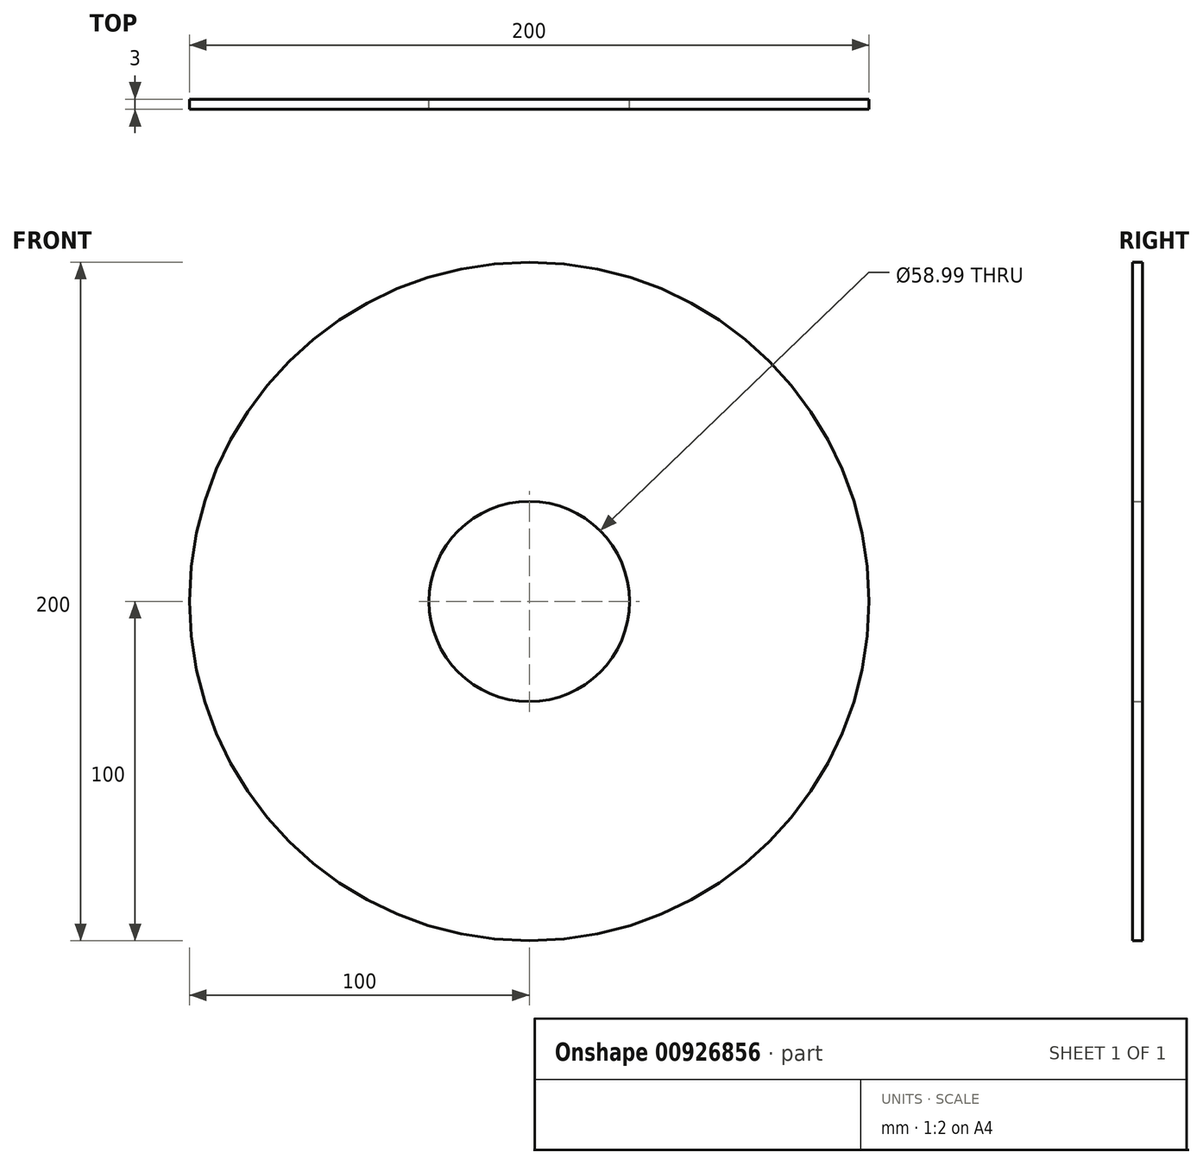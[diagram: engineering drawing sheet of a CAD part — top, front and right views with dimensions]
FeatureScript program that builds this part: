
annotation { "Feature Type Name" : "Feature", "Feature Type Description" : "" }
export const myFeature = defineFeature(function(context is Context, id is Id, definition is map)
    precondition{}
    {
        {
            var Q0;
            Q0=qCreatedBy(makeId("Front.planeOp"),FACE);
            var sketch = newSketch(context, id + "F0", { "sketchPlane" : qUnion([Q0])});
            skCircle(sketch, "E0", {"center": v(0, 0) * mm, "radius": 100 * mm});
            skCircle(sketch, "E1", {"center": v(0, 0) * mm, "radius": 29.5 * mm});
            skSolve(sketch);
        }
        {
            var Q0;
            Q0 = qSketchRegion(id + "F0", true);
            extrude(context, id + "F1", {"entities" : qUnion([Q0]), "depth" : 3 * mm, "offsetDistance" : 25 * mm});
        }
    });
